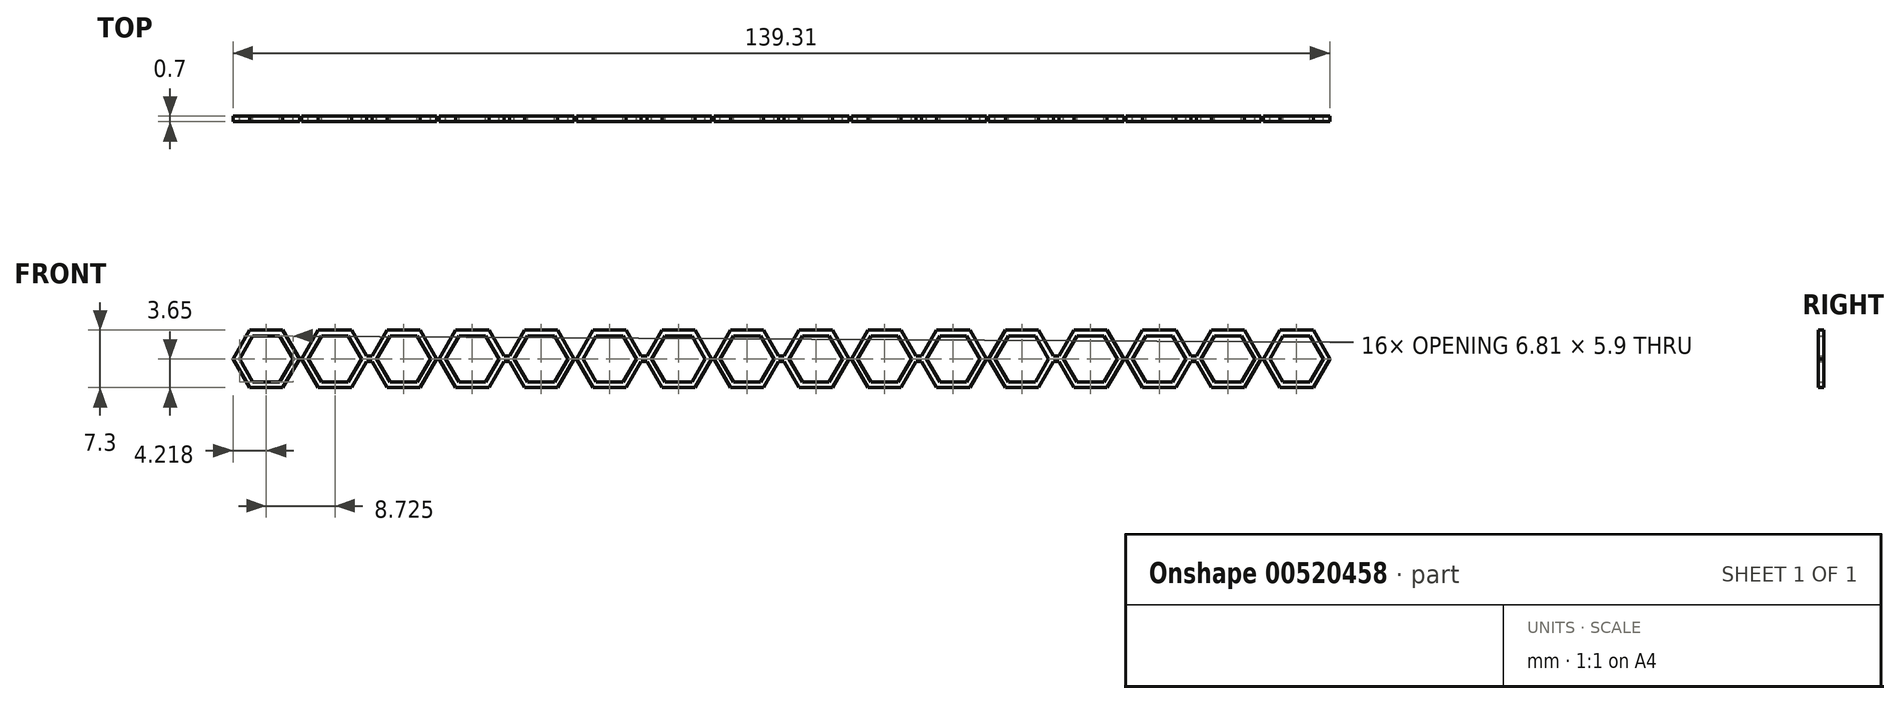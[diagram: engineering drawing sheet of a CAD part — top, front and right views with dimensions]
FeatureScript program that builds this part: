
annotation { "Feature Type Name" : "Feature", "Feature Type Description" : "" }
export const myFeature = defineFeature(function(context is Context, id is Id, definition is map)
    precondition{}
    {
        {
            var Q0;
            Q0=qCreatedBy(makeId("Front.planeOp"),FACE);
            var sketch = newSketch(context, id + "F0", { "sketchPlane" : qUnion([Q0])});
            skCircle(sketch, "E0.cCircle", {"center": v(0, 0) * mm, "radius": 2.95 * mm, "construction": true});
            skLineSegment(sketch, "E0.0", {"start": v(-1.7, 2.95) * mm, "end": v(1.7, 2.95) * mm});
            skLineSegment(sketch, "E0.1", {"start": v(1.7, 2.95) * mm, "end": v(3.4, 0) * mm});
            skLineSegment(sketch, "E0.2", {"start": v(3.4, 0) * mm, "end": v(1.7, -2.95) * mm});
            skLineSegment(sketch, "E0.3", {"start": v(1.7, -2.95) * mm, "end": v(-1.7, -2.95) * mm});
            skLineSegment(sketch, "E0.4", {"start": v(-1.7, -2.95) * mm, "end": v(-3.4, 0) * mm});
            skLineSegment(sketch, "E0.5", {"start": v(-3.4, 0) * mm, "end": v(-1.7, 2.95) * mm});
            skPoint(sketch, "E0.0.midPoint", {"position": v(0, 2.95) * mm});
            skCircle(sketch, "E1.cCircle", {"center": v(0, 0) * mm, "radius": 3.65 * mm, "construction": true});
            skLineSegment(sketch, "E1.0", {"start": v(-2.1, 3.65) * mm, "end": v(2.1, 3.65) * mm});
            skLineSegment(sketch, "E1.1", {"start": v(2.1, 3.65) * mm, "end": v(4.21, 0) * mm});
            skLineSegment(sketch, "E1.2", {"start": v(4.21, 0) * mm, "end": v(2.1, -3.65) * mm});
            skLineSegment(sketch, "E1.3", {"start": v(2.1, -3.65) * mm, "end": v(-2.1, -3.65) * mm});
            skLineSegment(sketch, "E1.4", {"start": v(-2.1, -3.65) * mm, "end": v(-4.21, 0) * mm});
            skLineSegment(sketch, "E1.5", {"start": v(-4.21, 0) * mm, "end": v(-2.1, 3.65) * mm});
            skPoint(sketch, "E1.0.midPoint", {"position": v(0, 3.65) * mm});
            skCircle(sketch, "E2.cCircle", {"center": v(8.73, 0) * mm, "radius": 2.95 * mm, "construction": true});
            skLineSegment(sketch, "E2.0", {"start": v(7.02, 2.95) * mm, "end": v(10.43, 2.95) * mm});
            skLineSegment(sketch, "E2.1", {"start": v(10.43, 2.95) * mm, "end": v(12.13, 0) * mm});
            skLineSegment(sketch, "E2.2", {"start": v(12.13, 0) * mm, "end": v(10.43, -2.95) * mm});
            skLineSegment(sketch, "E2.3", {"start": v(10.43, -2.95) * mm, "end": v(7.02, -2.95) * mm});
            skLineSegment(sketch, "E2.4", {"start": v(7.02, -2.95) * mm, "end": v(5.32, 0) * mm});
            skLineSegment(sketch, "E2.5", {"start": v(5.32, 0) * mm, "end": v(7.02, 2.95) * mm});
            skPoint(sketch, "E2.0.midPoint", {"position": v(8.73, 2.95) * mm});
            skCircle(sketch, "E3.cCircle", {"center": v(8.73, 0) * mm, "radius": 3.65 * mm, "construction": true});
            skLineSegment(sketch, "E3.0", {"start": v(6.62, 3.65) * mm, "end": v(10.83, 3.65) * mm});
            skLineSegment(sketch, "E3.1", {"start": v(10.83, 3.65) * mm, "end": v(12.94, 0) * mm});
            skLineSegment(sketch, "E3.2", {"start": v(12.94, 0) * mm, "end": v(10.83, -3.65) * mm});
            skLineSegment(sketch, "E3.3", {"start": v(10.83, -3.65) * mm, "end": v(6.62, -3.65) * mm});
            skLineSegment(sketch, "E3.4", {"start": v(6.62, -3.65) * mm, "end": v(4.51, 0) * mm});
            skLineSegment(sketch, "E3.5", {"start": v(4.51, 0) * mm, "end": v(6.62, 3.65) * mm});
            skPoint(sketch, "E3.0.midPoint", {"position": v(8.73, 3.65) * mm});
            skLineSegment(sketch, "E4", {"start": v(4.01, 0.35) * mm, "end": v(4.71, 0.35) * mm});
            skLineSegment(sketch, "E5", {"start": v(4.01, -0.35) * mm, "end": v(4.71, -0.35) * mm});
            skLineSegment(sketch, "E6", {"start": v(12.94, 0) * mm, "end": v(13.24, 0) * mm});
            skCircle(sketch, "E7.cCircle", {"center": v(17.45, 0) * mm, "radius": 2.95 * mm, "construction": true});
            skLineSegment(sketch, "E7.0", {"start": v(15.75, 2.95) * mm, "end": v(19.15, 2.95) * mm});
            skLineSegment(sketch, "E7.1", {"start": v(19.15, 2.95) * mm, "end": v(20.86, 0) * mm});
            skLineSegment(sketch, "E7.2", {"start": v(20.86, 0) * mm, "end": v(19.15, -2.95) * mm});
            skLineSegment(sketch, "E7.3", {"start": v(19.15, -2.95) * mm, "end": v(15.75, -2.95) * mm});
            skLineSegment(sketch, "E7.4", {"start": v(15.75, -2.95) * mm, "end": v(14.04, 0) * mm});
            skLineSegment(sketch, "E7.5", {"start": v(14.04, 0) * mm, "end": v(15.75, 2.95) * mm});
            skPoint(sketch, "E7.0.midPoint", {"position": v(17.45, 2.95) * mm});
            skCircle(sketch, "E8.cCircle", {"center": v(17.45, 0) * mm, "radius": 3.65 * mm, "construction": true});
            skLineSegment(sketch, "E8.0", {"start": v(15.34, 3.65) * mm, "end": v(19.56, 3.65) * mm});
            skLineSegment(sketch, "E8.1", {"start": v(19.56, 3.65) * mm, "end": v(21.67, 0) * mm});
            skLineSegment(sketch, "E8.2", {"start": v(21.67, 0) * mm, "end": v(19.56, -3.65) * mm});
            skLineSegment(sketch, "E8.3", {"start": v(19.56, -3.65) * mm, "end": v(15.34, -3.65) * mm});
            skLineSegment(sketch, "E8.4", {"start": v(15.34, -3.65) * mm, "end": v(13.24, 0) * mm});
            skLineSegment(sketch, "E8.5", {"start": v(13.24, 0) * mm, "end": v(15.34, 3.65) * mm});
            skPoint(sketch, "E8.0.midPoint", {"position": v(17.45, 3.65) * mm});
            skCircle(sketch, "E9.cCircle", {"center": v(26.18, 0) * mm, "radius": 2.95 * mm, "construction": true});
            skLineSegment(sketch, "E9.0", {"start": v(24.47, 2.95) * mm, "end": v(27.88, 2.95) * mm});
            skLineSegment(sketch, "E9.1", {"start": v(27.88, 2.95) * mm, "end": v(29.58, 0) * mm});
            skLineSegment(sketch, "E9.2", {"start": v(29.58, 0) * mm, "end": v(27.88, -2.95) * mm});
            skLineSegment(sketch, "E9.3", {"start": v(27.88, -2.95) * mm, "end": v(24.47, -2.95) * mm});
            skLineSegment(sketch, "E9.4", {"start": v(24.47, -2.95) * mm, "end": v(22.77, 0) * mm});
            skLineSegment(sketch, "E9.5", {"start": v(22.77, 0) * mm, "end": v(24.47, 2.95) * mm});
            skPoint(sketch, "E9.0.midPoint", {"position": v(26.18, 2.95) * mm});
            skCircle(sketch, "E10.cCircle", {"center": v(26.18, 0) * mm, "radius": 3.65 * mm, "construction": true});
            skLineSegment(sketch, "E10.0", {"start": v(24.07, 3.65) * mm, "end": v(28.28, 3.65) * mm});
            skLineSegment(sketch, "E10.1", {"start": v(28.28, 3.65) * mm, "end": v(30.4, 0) * mm});
            skLineSegment(sketch, "E10.2", {"start": v(30.4, 0) * mm, "end": v(28.28, -3.65) * mm});
            skLineSegment(sketch, "E10.3", {"start": v(28.28, -3.65) * mm, "end": v(24.07, -3.65) * mm});
            skLineSegment(sketch, "E10.4", {"start": v(24.07, -3.65) * mm, "end": v(21.96, 0) * mm});
            skLineSegment(sketch, "E10.5", {"start": v(21.96, 0) * mm, "end": v(24.07, 3.65) * mm});
            skPoint(sketch, "E10.0.midPoint", {"position": v(26.18, 3.65) * mm});
            skLineSegment(sketch, "E11", {"start": v(21.46, 0.35) * mm, "end": v(22.16, 0.35) * mm});
            skLineSegment(sketch, "E12", {"start": v(21.46, -0.35) * mm, "end": v(22.16, -0.35) * mm});
            skLineSegment(sketch, "E13", {"start": v(30.4, 0) * mm, "end": v(30.69, 0) * mm});
            skLineSegment(sketch, "E14", {"start": v(13.24, 0.35) * mm, "end": v(12.74, 0.35) * mm});
            skLineSegment(sketch, "E15", {"start": v(13.24, -0.35) * mm, "end": v(12.74, -0.35) * mm});
            skLineSegment(sketch, "E16", {"start": v(13.24, -0.35) * mm, "end": v(13.44, -0.35) * mm});
            skLineSegment(sketch, "E17", {"start": v(13.24, 0.35) * mm, "end": v(13.44, 0.35) * mm});
            skCircle(sketch, "E18.cCircle", {"center": v(34.9, 0) * mm, "radius": 2.95 * mm, "construction": true});
            skLineSegment(sketch, "E18.0", {"start": v(33.2, 2.95) * mm, "end": v(36.6, 2.95) * mm});
            skLineSegment(sketch, "E18.1", {"start": v(36.6, 2.95) * mm, "end": v(38.3, 0) * mm});
            skLineSegment(sketch, "E18.2", {"start": v(38.3, 0) * mm, "end": v(36.6, -2.95) * mm});
            skLineSegment(sketch, "E18.3", {"start": v(36.6, -2.95) * mm, "end": v(33.2, -2.95) * mm});
            skLineSegment(sketch, "E18.4", {"start": v(33.2, -2.95) * mm, "end": v(31.5, 0) * mm});
            skLineSegment(sketch, "E18.5", {"start": v(31.5, 0) * mm, "end": v(33.2, 2.95) * mm});
            skPoint(sketch, "E18.0.midPoint", {"position": v(34.9, 2.95) * mm});
            skCircle(sketch, "E19.cCircle", {"center": v(34.9, 0) * mm, "radius": 3.65 * mm, "construction": true});
            skLineSegment(sketch, "E19.0", {"start": v(32.8, 3.65) * mm, "end": v(37, 3.65) * mm});
            skLineSegment(sketch, "E19.1", {"start": v(37, 3.65) * mm, "end": v(39.12, 0) * mm});
            skLineSegment(sketch, "E19.2", {"start": v(39.12, 0) * mm, "end": v(37, -3.65) * mm});
            skLineSegment(sketch, "E19.3", {"start": v(37, -3.65) * mm, "end": v(32.8, -3.65) * mm});
            skLineSegment(sketch, "E19.4", {"start": v(32.8, -3.65) * mm, "end": v(30.69, 0) * mm});
            skLineSegment(sketch, "E19.5", {"start": v(30.69, 0) * mm, "end": v(32.8, 3.65) * mm});
            skPoint(sketch, "E19.0.midPoint", {"position": v(34.9, 3.65) * mm});
            skCircle(sketch, "E20.cCircle", {"center": v(43.63, 0) * mm, "radius": 2.95 * mm, "construction": true});
            skLineSegment(sketch, "E20.0", {"start": v(41.92, 2.95) * mm, "end": v(45.33, 2.95) * mm});
            skLineSegment(sketch, "E20.1", {"start": v(45.33, 2.95) * mm, "end": v(47.03, 0) * mm});
            skLineSegment(sketch, "E20.2", {"start": v(47.03, 0) * mm, "end": v(45.33, -2.95) * mm});
            skLineSegment(sketch, "E20.3", {"start": v(45.33, -2.95) * mm, "end": v(41.92, -2.95) * mm});
            skLineSegment(sketch, "E20.4", {"start": v(41.92, -2.95) * mm, "end": v(40.22, 0) * mm});
            skLineSegment(sketch, "E20.5", {"start": v(40.22, 0) * mm, "end": v(41.92, 2.95) * mm});
            skPoint(sketch, "E20.0.midPoint", {"position": v(43.63, 2.95) * mm});
            skCircle(sketch, "E21.cCircle", {"center": v(43.63, 0) * mm, "radius": 3.65 * mm, "construction": true});
            skLineSegment(sketch, "E21.0", {"start": v(41.52, 3.65) * mm, "end": v(45.73, 3.65) * mm});
            skLineSegment(sketch, "E21.1", {"start": v(45.73, 3.65) * mm, "end": v(47.84, 0) * mm});
            skLineSegment(sketch, "E21.2", {"start": v(47.84, 0) * mm, "end": v(45.73, -3.65) * mm});
            skLineSegment(sketch, "E21.3", {"start": v(45.73, -3.65) * mm, "end": v(41.52, -3.65) * mm});
            skLineSegment(sketch, "E21.4", {"start": v(41.52, -3.65) * mm, "end": v(39.41, 0) * mm});
            skLineSegment(sketch, "E21.5", {"start": v(39.41, 0) * mm, "end": v(41.52, 3.65) * mm});
            skPoint(sketch, "E21.0.midPoint", {"position": v(43.63, 3.65) * mm});
            skLineSegment(sketch, "E22", {"start": v(38.91, 0.35) * mm, "end": v(39.61, 0.35) * mm});
            skLineSegment(sketch, "E23", {"start": v(38.91, -0.35) * mm, "end": v(39.61, -0.35) * mm});
            skLineSegment(sketch, "E24", {"start": v(47.84, 0) * mm, "end": v(48.14, 0) * mm});
            skCircle(sketch, "E25.cCircle", {"center": v(52.35, 0) * mm, "radius": 2.95 * mm, "construction": true});
            skLineSegment(sketch, "E25.0", {"start": v(50.65, 2.95) * mm, "end": v(54.06, 2.95) * mm});
            skLineSegment(sketch, "E25.1", {"start": v(54.06, 2.95) * mm, "end": v(55.76, 0) * mm});
            skLineSegment(sketch, "E25.2", {"start": v(55.76, 0) * mm, "end": v(54.06, -2.95) * mm});
            skLineSegment(sketch, "E25.3", {"start": v(54.06, -2.95) * mm, "end": v(50.65, -2.95) * mm});
            skLineSegment(sketch, "E25.4", {"start": v(50.65, -2.95) * mm, "end": v(48.95, 0) * mm});
            skLineSegment(sketch, "E25.5", {"start": v(48.95, 0) * mm, "end": v(50.65, 2.95) * mm});
            skPoint(sketch, "E25.0.midPoint", {"position": v(52.35, 2.95) * mm});
            skCircle(sketch, "E26.cCircle", {"center": v(52.35, 0) * mm, "radius": 3.65 * mm, "construction": true});
            skLineSegment(sketch, "E26.0", {"start": v(50.24, 3.65) * mm, "end": v(54.46, 3.65) * mm});
            skLineSegment(sketch, "E26.1", {"start": v(54.46, 3.65) * mm, "end": v(56.57, 0) * mm});
            skLineSegment(sketch, "E26.2", {"start": v(56.57, 0) * mm, "end": v(54.46, -3.65) * mm});
            skLineSegment(sketch, "E26.3", {"start": v(54.46, -3.65) * mm, "end": v(50.24, -3.65) * mm});
            skLineSegment(sketch, "E26.4", {"start": v(50.24, -3.65) * mm, "end": v(48.14, 0) * mm});
            skLineSegment(sketch, "E26.5", {"start": v(48.14, 0) * mm, "end": v(50.24, 3.65) * mm});
            skPoint(sketch, "E26.0.midPoint", {"position": v(52.35, 3.65) * mm});
            skCircle(sketch, "E27.cCircle", {"center": v(61.08, 0) * mm, "radius": 2.95 * mm, "construction": true});
            skLineSegment(sketch, "E27.0", {"start": v(59.37, 2.95) * mm, "end": v(62.78, 2.95) * mm});
            skLineSegment(sketch, "E27.1", {"start": v(62.78, 2.95) * mm, "end": v(64.48, 0) * mm});
            skLineSegment(sketch, "E27.2", {"start": v(64.48, 0) * mm, "end": v(62.78, -2.95) * mm});
            skLineSegment(sketch, "E27.3", {"start": v(62.78, -2.95) * mm, "end": v(59.37, -2.95) * mm});
            skLineSegment(sketch, "E27.4", {"start": v(59.37, -2.95) * mm, "end": v(57.67, 0) * mm});
            skLineSegment(sketch, "E27.5", {"start": v(57.67, 0) * mm, "end": v(59.37, 2.95) * mm});
            skPoint(sketch, "E27.0.midPoint", {"position": v(61.08, 2.95) * mm});
            skCircle(sketch, "E28.cCircle", {"center": v(61.08, 0) * mm, "radius": 3.65 * mm, "construction": true});
            skLineSegment(sketch, "E28.0", {"start": v(58.97, 3.65) * mm, "end": v(63.18, 3.65) * mm});
            skLineSegment(sketch, "E28.1", {"start": v(63.18, 3.65) * mm, "end": v(65.3, 0) * mm});
            skLineSegment(sketch, "E28.2", {"start": v(65.3, 0) * mm, "end": v(63.18, -3.65) * mm});
            skLineSegment(sketch, "E28.3", {"start": v(63.18, -3.65) * mm, "end": v(58.97, -3.65) * mm});
            skLineSegment(sketch, "E28.4", {"start": v(58.97, -3.65) * mm, "end": v(56.86, 0) * mm});
            skLineSegment(sketch, "E28.5", {"start": v(56.86, 0) * mm, "end": v(58.97, 3.65) * mm});
            skPoint(sketch, "E28.0.midPoint", {"position": v(61.08, 3.65) * mm});
            skLineSegment(sketch, "E29", {"start": v(56.36, 0.35) * mm, "end": v(57.06, 0.35) * mm});
            skLineSegment(sketch, "E30", {"start": v(56.36, -0.35) * mm, "end": v(57.06, -0.35) * mm});
            skLineSegment(sketch, "E31", {"start": v(65.3, 0) * mm, "end": v(65.59, 0) * mm});
            skLineSegment(sketch, "E32", {"start": v(65.59, 0) * mm, "end": v(65.59, 0.35) * mm});
            skLineSegment(sketch, "E33", {"start": v(65.59, 0) * mm, "end": v(65.59, -0.35) * mm});
            skLineSegment(sketch, "E34", {"start": v(48.14, 0.35) * mm, "end": v(47.64, 0.35) * mm});
            skLineSegment(sketch, "E35", {"start": v(48.14, -0.35) * mm, "end": v(47.64, -0.35) * mm});
            skLineSegment(sketch, "E36", {"start": v(48.14, -0.35) * mm, "end": v(48.34, -0.35) * mm});
            skLineSegment(sketch, "E37", {"start": v(48.14, 0.35) * mm, "end": v(48.34, 0.35) * mm});
            skLineSegment(sketch, "E38", {"start": v(30.69, 0.35) * mm, "end": v(30.19, 0.35) * mm});
            skLineSegment(sketch, "E39", {"start": v(30.69, -0.35) * mm, "end": v(30.19, -0.35) * mm});
            skLineSegment(sketch, "E40", {"start": v(30.69, -0.35) * mm, "end": v(30.89, -0.35) * mm});
            skLineSegment(sketch, "E41", {"start": v(30.69, 0.35) * mm, "end": v(30.89, 0.35) * mm});
            skCircle(sketch, "E42.cCircle", {"center": v(-69.8, 0) * mm, "radius": 2.95 * mm, "construction": true});
            skLineSegment(sketch, "E42.0", {"start": v(-71.5, 2.95) * mm, "end": v(-68.1, 2.95) * mm});
            skLineSegment(sketch, "E42.1", {"start": v(-68.1, 2.95) * mm, "end": v(-66.4, 0) * mm});
            skLineSegment(sketch, "E42.2", {"start": v(-66.4, 0) * mm, "end": v(-68.1, -2.95) * mm});
            skLineSegment(sketch, "E42.3", {"start": v(-68.1, -2.95) * mm, "end": v(-71.5, -2.95) * mm});
            skLineSegment(sketch, "E42.4", {"start": v(-71.5, -2.95) * mm, "end": v(-73.2, 0) * mm});
            skLineSegment(sketch, "E42.5", {"start": v(-73.2, 0) * mm, "end": v(-71.5, 2.95) * mm});
            skPoint(sketch, "E42.0.midPoint", {"position": v(-69.8, 2.95) * mm});
            skCircle(sketch, "E43.cCircle", {"center": v(-69.8, 0) * mm, "radius": 3.65 * mm, "construction": true});
            skLineSegment(sketch, "E43.0", {"start": v(-71.9, 3.65) * mm, "end": v(-67.7, 3.65) * mm});
            skLineSegment(sketch, "E43.1", {"start": v(-67.7, 3.65) * mm, "end": v(-65.59, 0) * mm});
            skLineSegment(sketch, "E43.2", {"start": v(-65.59, 0) * mm, "end": v(-67.7, -3.65) * mm});
            skLineSegment(sketch, "E43.3", {"start": v(-67.7, -3.65) * mm, "end": v(-71.9, -3.65) * mm});
            skLineSegment(sketch, "E43.4", {"start": v(-71.9, -3.65) * mm, "end": v(-74.02, 0) * mm});
            skLineSegment(sketch, "E43.5", {"start": v(-74.02, 0) * mm, "end": v(-71.9, 3.65) * mm});
            skPoint(sketch, "E43.0.midPoint", {"position": v(-69.8, 3.65) * mm});
            skCircle(sketch, "E44.cCircle", {"center": v(-61.08, 0) * mm, "radius": 2.95 * mm, "construction": true});
            skLineSegment(sketch, "E44.0", {"start": v(-62.78, 2.95) * mm, "end": v(-59.37, 2.95) * mm});
            skLineSegment(sketch, "E44.1", {"start": v(-59.37, 2.95) * mm, "end": v(-57.67, 0) * mm});
            skLineSegment(sketch, "E44.2", {"start": v(-57.67, 0) * mm, "end": v(-59.37, -2.95) * mm});
            skLineSegment(sketch, "E44.3", {"start": v(-59.37, -2.95) * mm, "end": v(-62.78, -2.95) * mm});
            skLineSegment(sketch, "E44.4", {"start": v(-62.78, -2.95) * mm, "end": v(-64.48, 0) * mm});
            skLineSegment(sketch, "E44.5", {"start": v(-64.48, 0) * mm, "end": v(-62.78, 2.95) * mm});
            skPoint(sketch, "E44.0.midPoint", {"position": v(-61.08, 2.95) * mm});
            skCircle(sketch, "E45.cCircle", {"center": v(-61.08, 0) * mm, "radius": 3.65 * mm, "construction": true});
            skLineSegment(sketch, "E45.0", {"start": v(-63.18, 3.65) * mm, "end": v(-58.97, 3.65) * mm});
            skLineSegment(sketch, "E45.1", {"start": v(-58.97, 3.65) * mm, "end": v(-56.86, 0) * mm});
            skLineSegment(sketch, "E45.2", {"start": v(-56.86, 0) * mm, "end": v(-58.97, -3.65) * mm});
            skLineSegment(sketch, "E45.3", {"start": v(-58.97, -3.65) * mm, "end": v(-63.18, -3.65) * mm});
            skLineSegment(sketch, "E45.4", {"start": v(-63.18, -3.65) * mm, "end": v(-65.3, 0) * mm});
            skLineSegment(sketch, "E45.5", {"start": v(-65.3, 0) * mm, "end": v(-63.18, 3.65) * mm});
            skPoint(sketch, "E45.0.midPoint", {"position": v(-61.08, 3.65) * mm});
            skLineSegment(sketch, "E46", {"start": v(-65.79, 0.35) * mm, "end": v(-65.09, 0.35) * mm});
            skLineSegment(sketch, "E47", {"start": v(-65.79, -0.35) * mm, "end": v(-65.09, -0.35) * mm});
            skLineSegment(sketch, "E48", {"start": v(-56.86, 0) * mm, "end": v(-56.57, 0) * mm});
            skCircle(sketch, "E49.cCircle", {"center": v(-52.35, 0) * mm, "radius": 2.95 * mm, "construction": true});
            skLineSegment(sketch, "E49.0", {"start": v(-54.05, 2.95) * mm, "end": v(-50.65, 2.95) * mm});
            skLineSegment(sketch, "E49.1", {"start": v(-50.65, 2.95) * mm, "end": v(-48.95, 0) * mm});
            skLineSegment(sketch, "E49.2", {"start": v(-48.95, 0) * mm, "end": v(-50.65, -2.95) * mm});
            skLineSegment(sketch, "E49.3", {"start": v(-50.65, -2.95) * mm, "end": v(-54.05, -2.95) * mm});
            skLineSegment(sketch, "E49.4", {"start": v(-54.05, -2.95) * mm, "end": v(-55.76, 0) * mm});
            skLineSegment(sketch, "E49.5", {"start": v(-55.76, 0) * mm, "end": v(-54.05, 2.95) * mm});
            skPoint(sketch, "E49.0.midPoint", {"position": v(-52.35, 2.95) * mm});
            skCircle(sketch, "E50.cCircle", {"center": v(-52.35, 0) * mm, "radius": 3.65 * mm, "construction": true});
            skLineSegment(sketch, "E50.0", {"start": v(-54.46, 3.65) * mm, "end": v(-50.24, 3.65) * mm});
            skLineSegment(sketch, "E50.1", {"start": v(-50.24, 3.65) * mm, "end": v(-48.14, 0) * mm});
            skLineSegment(sketch, "E50.2", {"start": v(-48.14, 0) * mm, "end": v(-50.24, -3.65) * mm});
            skLineSegment(sketch, "E50.3", {"start": v(-50.24, -3.65) * mm, "end": v(-54.46, -3.65) * mm});
            skLineSegment(sketch, "E50.4", {"start": v(-54.46, -3.65) * mm, "end": v(-56.57, 0) * mm});
            skLineSegment(sketch, "E50.5", {"start": v(-56.57, 0) * mm, "end": v(-54.46, 3.65) * mm});
            skPoint(sketch, "E50.0.midPoint", {"position": v(-52.35, 3.65) * mm});
            skCircle(sketch, "E51.cCircle", {"center": v(-43.63, 0) * mm, "radius": 2.95 * mm, "construction": true});
            skLineSegment(sketch, "E51.0", {"start": v(-45.33, 2.95) * mm, "end": v(-41.92, 2.95) * mm});
            skLineSegment(sketch, "E51.1", {"start": v(-41.92, 2.95) * mm, "end": v(-40.22, 0) * mm});
            skLineSegment(sketch, "E51.2", {"start": v(-40.22, 0) * mm, "end": v(-41.92, -2.95) * mm});
            skLineSegment(sketch, "E51.3", {"start": v(-41.92, -2.95) * mm, "end": v(-45.33, -2.95) * mm});
            skLineSegment(sketch, "E51.4", {"start": v(-45.33, -2.95) * mm, "end": v(-47.03, 0) * mm});
            skLineSegment(sketch, "E51.5", {"start": v(-47.03, 0) * mm, "end": v(-45.33, 2.95) * mm});
            skPoint(sketch, "E51.0.midPoint", {"position": v(-43.63, 2.95) * mm});
            skCircle(sketch, "E52.cCircle", {"center": v(-43.63, 0) * mm, "radius": 3.65 * mm, "construction": true});
            skLineSegment(sketch, "E52.0", {"start": v(-45.73, 3.65) * mm, "end": v(-41.52, 3.65) * mm});
            skLineSegment(sketch, "E52.1", {"start": v(-41.52, 3.65) * mm, "end": v(-39.41, 0) * mm});
            skLineSegment(sketch, "E52.2", {"start": v(-39.41, 0) * mm, "end": v(-41.52, -3.65) * mm});
            skLineSegment(sketch, "E52.3", {"start": v(-41.52, -3.65) * mm, "end": v(-45.73, -3.65) * mm});
            skLineSegment(sketch, "E52.4", {"start": v(-45.73, -3.65) * mm, "end": v(-47.84, 0) * mm});
            skLineSegment(sketch, "E52.5", {"start": v(-47.84, 0) * mm, "end": v(-45.73, 3.65) * mm});
            skPoint(sketch, "E52.0.midPoint", {"position": v(-43.63, 3.65) * mm});
            skLineSegment(sketch, "E53", {"start": v(-48.34, 0.35) * mm, "end": v(-47.64, 0.35) * mm});
            skLineSegment(sketch, "E54", {"start": v(-48.34, -0.35) * mm, "end": v(-47.64, -0.35) * mm});
            skLineSegment(sketch, "E55", {"start": v(-39.41, 0) * mm, "end": v(-39.12, 0) * mm});
            skLineSegment(sketch, "E56", {"start": v(-56.57, 0.35) * mm, "end": v(-57.06, 0.35) * mm});
            skLineSegment(sketch, "E57", {"start": v(-56.57, -0.35) * mm, "end": v(-57.06, -0.35) * mm});
            skLineSegment(sketch, "E58", {"start": v(-56.57, -0.35) * mm, "end": v(-56.36, -0.35) * mm});
            skLineSegment(sketch, "E59", {"start": v(-56.57, 0.35) * mm, "end": v(-56.36, 0.35) * mm});
            skCircle(sketch, "E60.cCircle", {"center": v(-34.9, 0) * mm, "radius": 2.95 * mm, "construction": true});
            skLineSegment(sketch, "E60.0", {"start": v(-36.6, 2.95) * mm, "end": v(-33.2, 2.95) * mm});
            skLineSegment(sketch, "E60.1", {"start": v(-33.2, 2.95) * mm, "end": v(-31.5, 0) * mm});
            skLineSegment(sketch, "E60.2", {"start": v(-31.5, 0) * mm, "end": v(-33.2, -2.95) * mm});
            skLineSegment(sketch, "E60.3", {"start": v(-33.2, -2.95) * mm, "end": v(-36.6, -2.95) * mm});
            skLineSegment(sketch, "E60.4", {"start": v(-36.6, -2.95) * mm, "end": v(-38.3, 0) * mm});
            skLineSegment(sketch, "E60.5", {"start": v(-38.3, 0) * mm, "end": v(-36.6, 2.95) * mm});
            skPoint(sketch, "E60.0.midPoint", {"position": v(-34.9, 2.95) * mm});
            skCircle(sketch, "E61.cCircle", {"center": v(-34.9, 0) * mm, "radius": 3.65 * mm, "construction": true});
            skLineSegment(sketch, "E61.0", {"start": v(-37, 3.65) * mm, "end": v(-32.8, 3.65) * mm});
            skLineSegment(sketch, "E61.1", {"start": v(-32.8, 3.65) * mm, "end": v(-30.69, 0) * mm});
            skLineSegment(sketch, "E61.2", {"start": v(-30.69, 0) * mm, "end": v(-32.8, -3.65) * mm});
            skLineSegment(sketch, "E61.3", {"start": v(-32.8, -3.65) * mm, "end": v(-37, -3.65) * mm});
            skLineSegment(sketch, "E61.4", {"start": v(-37, -3.65) * mm, "end": v(-39.12, 0) * mm});
            skLineSegment(sketch, "E61.5", {"start": v(-39.12, 0) * mm, "end": v(-37, 3.65) * mm});
            skPoint(sketch, "E61.0.midPoint", {"position": v(-34.9, 3.65) * mm});
            skCircle(sketch, "E62.cCircle", {"center": v(-26.18, 0) * mm, "radius": 2.95 * mm, "construction": true});
            skLineSegment(sketch, "E62.0", {"start": v(-27.88, 2.95) * mm, "end": v(-24.47, 2.95) * mm});
            skLineSegment(sketch, "E62.1", {"start": v(-24.47, 2.95) * mm, "end": v(-22.77, 0) * mm});
            skLineSegment(sketch, "E62.2", {"start": v(-22.77, 0) * mm, "end": v(-24.47, -2.95) * mm});
            skLineSegment(sketch, "E62.3", {"start": v(-24.47, -2.95) * mm, "end": v(-27.88, -2.95) * mm});
            skLineSegment(sketch, "E62.4", {"start": v(-27.88, -2.95) * mm, "end": v(-29.58, 0) * mm});
            skLineSegment(sketch, "E62.5", {"start": v(-29.58, 0) * mm, "end": v(-27.88, 2.95) * mm});
            skPoint(sketch, "E62.0.midPoint", {"position": v(-26.18, 2.95) * mm});
            skCircle(sketch, "E63.cCircle", {"center": v(-26.18, 0) * mm, "radius": 3.65 * mm, "construction": true});
            skLineSegment(sketch, "E63.0", {"start": v(-28.28, 3.65) * mm, "end": v(-24.07, 3.65) * mm});
            skLineSegment(sketch, "E63.1", {"start": v(-24.07, 3.65) * mm, "end": v(-21.96, 0) * mm});
            skLineSegment(sketch, "E63.2", {"start": v(-21.96, 0) * mm, "end": v(-24.07, -3.65) * mm});
            skLineSegment(sketch, "E63.3", {"start": v(-24.07, -3.65) * mm, "end": v(-28.28, -3.65) * mm});
            skLineSegment(sketch, "E63.4", {"start": v(-28.28, -3.65) * mm, "end": v(-30.4, 0) * mm});
            skLineSegment(sketch, "E63.5", {"start": v(-30.4, 0) * mm, "end": v(-28.28, 3.65) * mm});
            skPoint(sketch, "E63.0.midPoint", {"position": v(-26.18, 3.65) * mm});
            skLineSegment(sketch, "E64", {"start": v(-30.89, 0.35) * mm, "end": v(-30.19, 0.35) * mm});
            skLineSegment(sketch, "E65", {"start": v(-30.89, -0.35) * mm, "end": v(-30.19, -0.35) * mm});
            skLineSegment(sketch, "E66", {"start": v(-21.96, 0) * mm, "end": v(-21.66, 0) * mm});
            skCircle(sketch, "E67.cCircle", {"center": v(-17.45, 0) * mm, "radius": 2.95 * mm, "construction": true});
            skLineSegment(sketch, "E67.0", {"start": v(-19.15, 2.95) * mm, "end": v(-15.75, 2.95) * mm});
            skLineSegment(sketch, "E67.1", {"start": v(-15.75, 2.95) * mm, "end": v(-14.04, 0) * mm});
            skLineSegment(sketch, "E67.2", {"start": v(-14.04, 0) * mm, "end": v(-15.75, -2.95) * mm});
            skLineSegment(sketch, "E67.3", {"start": v(-15.75, -2.95) * mm, "end": v(-19.15, -2.95) * mm});
            skLineSegment(sketch, "E67.4", {"start": v(-19.15, -2.95) * mm, "end": v(-20.86, 0) * mm});
            skLineSegment(sketch, "E67.5", {"start": v(-20.86, 0) * mm, "end": v(-19.15, 2.95) * mm});
            skPoint(sketch, "E67.0.midPoint", {"position": v(-17.45, 2.95) * mm});
            skCircle(sketch, "E68.cCircle", {"center": v(-17.45, 0) * mm, "radius": 3.65 * mm, "construction": true});
            skLineSegment(sketch, "E68.0", {"start": v(-19.56, 3.65) * mm, "end": v(-15.34, 3.65) * mm});
            skLineSegment(sketch, "E68.1", {"start": v(-15.34, 3.65) * mm, "end": v(-13.24, 0) * mm});
            skLineSegment(sketch, "E68.2", {"start": v(-13.24, 0) * mm, "end": v(-15.34, -3.65) * mm});
            skLineSegment(sketch, "E68.3", {"start": v(-15.34, -3.65) * mm, "end": v(-19.56, -3.65) * mm});
            skLineSegment(sketch, "E68.4", {"start": v(-19.56, -3.65) * mm, "end": v(-21.66, 0) * mm});
            skLineSegment(sketch, "E68.5", {"start": v(-21.66, 0) * mm, "end": v(-19.56, 3.65) * mm});
            skPoint(sketch, "E68.0.midPoint", {"position": v(-17.45, 3.65) * mm});
            skCircle(sketch, "E69.cCircle", {"center": v(-8.72, 0) * mm, "radius": 2.95 * mm, "construction": true});
            skLineSegment(sketch, "E69.0", {"start": v(-10.43, 2.95) * mm, "end": v(-7.02, 2.95) * mm});
            skLineSegment(sketch, "E69.1", {"start": v(-7.02, 2.95) * mm, "end": v(-5.32, 0) * mm});
            skLineSegment(sketch, "E69.2", {"start": v(-5.32, 0) * mm, "end": v(-7.02, -2.95) * mm});
            skLineSegment(sketch, "E69.3", {"start": v(-7.02, -2.95) * mm, "end": v(-10.43, -2.95) * mm});
            skLineSegment(sketch, "E69.4", {"start": v(-10.43, -2.95) * mm, "end": v(-12.13, 0) * mm});
            skLineSegment(sketch, "E69.5", {"start": v(-12.13, 0) * mm, "end": v(-10.43, 2.95) * mm});
            skPoint(sketch, "E69.0.midPoint", {"position": v(-8.72, 2.95) * mm});
            skCircle(sketch, "E70.cCircle", {"center": v(-8.72, 0) * mm, "radius": 3.65 * mm, "construction": true});
            skLineSegment(sketch, "E70.0", {"start": v(-10.83, 3.65) * mm, "end": v(-6.62, 3.65) * mm});
            skLineSegment(sketch, "E70.1", {"start": v(-6.62, 3.65) * mm, "end": v(-4.51, 0) * mm});
            skLineSegment(sketch, "E70.2", {"start": v(-4.51, 0) * mm, "end": v(-6.62, -3.65) * mm});
            skLineSegment(sketch, "E70.3", {"start": v(-6.62, -3.65) * mm, "end": v(-10.83, -3.65) * mm});
            skLineSegment(sketch, "E70.4", {"start": v(-10.83, -3.65) * mm, "end": v(-12.94, 0) * mm});
            skLineSegment(sketch, "E70.5", {"start": v(-12.94, 0) * mm, "end": v(-10.83, 3.65) * mm});
            skPoint(sketch, "E70.0.midPoint", {"position": v(-8.72, 3.65) * mm});
            skLineSegment(sketch, "E71", {"start": v(-13.44, 0.35) * mm, "end": v(-12.74, 0.35) * mm});
            skLineSegment(sketch, "E72", {"start": v(-13.44, -0.35) * mm, "end": v(-12.74, -0.35) * mm});
            skLineSegment(sketch, "E73", {"start": v(-4.51, 0) * mm, "end": v(-4.21, 0) * mm});
            skLineSegment(sketch, "E74", {"start": v(-21.66, 0.35) * mm, "end": v(-22.16, 0.35) * mm});
            skLineSegment(sketch, "E75", {"start": v(-21.66, -0.35) * mm, "end": v(-22.16, -0.35) * mm});
            skLineSegment(sketch, "E76", {"start": v(-21.66, -0.35) * mm, "end": v(-21.46, -0.35) * mm});
            skLineSegment(sketch, "E77", {"start": v(-21.66, 0.35) * mm, "end": v(-21.46, 0.35) * mm});
            skLineSegment(sketch, "E78", {"start": v(-39.12, 0.35) * mm, "end": v(-39.61, 0.35) * mm});
            skLineSegment(sketch, "E79", {"start": v(-39.12, -0.35) * mm, "end": v(-39.61, -0.35) * mm});
            skLineSegment(sketch, "E80", {"start": v(-39.12, -0.35) * mm, "end": v(-38.91, -0.35) * mm});
            skLineSegment(sketch, "E81", {"start": v(-39.12, 0.35) * mm, "end": v(-38.91, 0.35) * mm});
            skLineSegment(sketch, "E82", {"start": v(-4.21, 0.35) * mm, "end": v(-4.71, 0.35) * mm});
            skLineSegment(sketch, "E83", {"start": v(-4.21, 0.35) * mm, "end": v(-4.01, 0.35) * mm});
            skLineSegment(sketch, "E84", {"start": v(-4.21, -0.35) * mm, "end": v(-4.01, -0.35) * mm});
            skLineSegment(sketch, "E85", {"start": v(-4.21, -0.35) * mm, "end": v(-4.71, -0.35) * mm});
            skSolve(sketch);
        }
        {
            var Q0;
            Q0=makeQuery(id+"F0.imprint","IMPRINT",FACE,{"disambiguationData":[TD([[makeQuery(id+"F0.imprint","IMPRINT",EDGE,{"derivedFrom":sQuery(id+"F0.wireOp",EDGE,"E42.0")}),1.0]])]});
            var Q1;
            Q1=makeQuery(id+"F0.imprint","IMPRINT",FACE,{"disambiguationData":[TD([[makeQuery(id+"F0.imprint","IMPRINT",EDGE,{"derivedFrom":sQuery(id+"F0.wireOp",EDGE,"E44.0")}),1.0]])]});
            var Q2;
            {var subQ7=sQuery(id+"F0.wireOp",EDGE,"E46");Q2=makeQuery(id+"F0.imprint","IMPRINT",FACE,{"disambiguationData":[TD([[makeQuery(id+"F0.imprint","IMPRINT",EDGE,{"derivedFrom":subQ7}),-1.0]])]});}
            var Q3;
            {var subQ2=sQuery(id+"F0.wireOp",EDGE,"E48");Q3=makeQuery(id+"F0.imprint","IMPRINT",FACE,{"disambiguationData":[TD([[makeQuery(id+"F0.imprint","IMPRINT",EDGE,{"derivedFrom":subQ2}),-1.0]])]});}
            var Q4;
            {var subQ2=sQuery(id+"F0.wireOp",EDGE,"E48");Q4=makeQuery(id+"F0.imprint","IMPRINT",FACE,{"disambiguationData":[TD([[makeQuery(id+"F0.imprint","IMPRINT",EDGE,{"derivedFrom":subQ2}),1.0]])]});}
            var Q5;
            Q5=makeQuery(id+"F0.imprint","IMPRINT",FACE,{"disambiguationData":[TD([[makeQuery(id+"F0.imprint","IMPRINT",EDGE,{"derivedFrom":sQuery(id+"F0.wireOp",EDGE,"E49.0")}),1.0]])]});
            var Q6;
            {var subQ3=sQuery(id+"F0.wireOp",EDGE,"E53");Q6=makeQuery(id+"F0.imprint","IMPRINT",FACE,{"disambiguationData":[TD([[makeQuery(id+"F0.imprint","IMPRINT",EDGE,{"derivedFrom":subQ3}),-1.0]])]});}
            var Q7;
            Q7=makeQuery(id+"F0.imprint","IMPRINT",FACE,{"disambiguationData":[TD([[makeQuery(id+"F0.imprint","IMPRINT",EDGE,{"derivedFrom":sQuery(id+"F0.wireOp",EDGE,"E51.0")}),1.0]])]});
            var Q8;
            {var subQ1=sQuery(id+"F0.wireOp",EDGE,"E55");Q8=makeQuery(id+"F0.imprint","IMPRINT",FACE,{"disambiguationData":[TD([[makeQuery(id+"F0.imprint","IMPRINT",EDGE,{"derivedFrom":subQ1}),-1.0]])]});}
            var Q9;
            {var subQ2=sQuery(id+"F0.wireOp",EDGE,"E55");Q9=makeQuery(id+"F0.imprint","IMPRINT",FACE,{"disambiguationData":[TD([[makeQuery(id+"F0.imprint","IMPRINT",EDGE,{"derivedFrom":subQ2}),1.0]])]});}
            var Q10;
            Q10=makeQuery(id+"F0.imprint","IMPRINT",FACE,{"disambiguationData":[TD([[makeQuery(id+"F0.imprint","IMPRINT",EDGE,{"derivedFrom":sQuery(id+"F0.wireOp",EDGE,"E60.0")}),1.0]])]});
            var Q11;
            {var subQ3=sQuery(id+"F0.wireOp",EDGE,"E64");Q11=makeQuery(id+"F0.imprint","IMPRINT",FACE,{"disambiguationData":[TD([[makeQuery(id+"F0.imprint","IMPRINT",EDGE,{"derivedFrom":subQ3}),-1.0]])]});}
            var Q12;
            Q12=makeQuery(id+"F0.imprint","IMPRINT",FACE,{"disambiguationData":[TD([[makeQuery(id+"F0.imprint","IMPRINT",EDGE,{"derivedFrom":sQuery(id+"F0.wireOp",EDGE,"E62.0")}),1.0]])]});
            var Q13;
            {var subQ2=sQuery(id+"F0.wireOp",EDGE,"E66");Q13=makeQuery(id+"F0.imprint","IMPRINT",FACE,{"disambiguationData":[TD([[makeQuery(id+"F0.imprint","IMPRINT",EDGE,{"derivedFrom":subQ2}),1.0]])]});}
            var Q14;
            {var subQ2=sQuery(id+"F0.wireOp",EDGE,"E66");Q14=makeQuery(id+"F0.imprint","IMPRINT",FACE,{"disambiguationData":[TD([[makeQuery(id+"F0.imprint","IMPRINT",EDGE,{"derivedFrom":subQ2}),-1.0]])]});}
            var Q15;
            Q15=makeQuery(id+"F0.imprint","IMPRINT",FACE,{"disambiguationData":[TD([[makeQuery(id+"F0.imprint","IMPRINT",EDGE,{"derivedFrom":sQuery(id+"F0.wireOp",EDGE,"E67.0")}),1.0]])]});
            var Q16;
            Q16=makeQuery(id+"F0.imprint","IMPRINT",FACE,{"disambiguationData":[TD([[makeQuery(id+"F0.imprint","IMPRINT",EDGE,{"derivedFrom":sQuery(id+"F0.wireOp",EDGE,"E69.0")}),1.0]])]});
            var Q17;
            {var subQ3=sQuery(id+"F0.wireOp",EDGE,"E71");Q17=makeQuery(id+"F0.imprint","IMPRINT",FACE,{"disambiguationData":[TD([[makeQuery(id+"F0.imprint","IMPRINT",EDGE,{"derivedFrom":subQ3}),-1.0]])]});}
            var Q18;
            {var subQ5=sQuery(id+"F0.wireOp",EDGE,"E82");Q18=makeQuery(id+"F0.imprint","IMPRINT",FACE,{"disambiguationData":[TD([[makeQuery(id+"F0.imprint","IMPRINT",EDGE,{"derivedFrom":subQ5}),1.0]])]});}
            var Q19;
            {var subQ5=sQuery(id+"F0.wireOp",EDGE,"E84");Q19=makeQuery(id+"F0.imprint","IMPRINT",FACE,{"disambiguationData":[TD([[makeQuery(id+"F0.imprint","IMPRINT",EDGE,{"derivedFrom":subQ5}),1.0]])]});}
            var Q20;
            Q20=makeQuery(id+"F0.imprint","IMPRINT",FACE,{"disambiguationData":[TD([[makeQuery(id+"F0.imprint","IMPRINT",EDGE,{"derivedFrom":sQuery(id+"F0.wireOp",EDGE,"E0.0")}),1.0]])]});
            var Q21;
            {var subQ3=sQuery(id+"F0.wireOp",EDGE,"E4");Q21=makeQuery(id+"F0.imprint","IMPRINT",FACE,{"disambiguationData":[TD([[makeQuery(id+"F0.imprint","IMPRINT",EDGE,{"derivedFrom":subQ3}),-1.0]])]});}
            var Q22;
            Q22=makeQuery(id+"F0.imprint","IMPRINT",FACE,{"disambiguationData":[TD([[makeQuery(id+"F0.imprint","IMPRINT",EDGE,{"derivedFrom":sQuery(id+"F0.wireOp",EDGE,"E2.0")}),1.0]])]});
            var Q23;
            {var subQ2=sQuery(id+"F0.wireOp",EDGE,"E6");Q23=makeQuery(id+"F0.imprint","IMPRINT",FACE,{"disambiguationData":[TD([[makeQuery(id+"F0.imprint","IMPRINT",EDGE,{"derivedFrom":subQ2}),1.0]])]});}
            var Q24;
            {var subQ2=sQuery(id+"F0.wireOp",EDGE,"E6");Q24=makeQuery(id+"F0.imprint","IMPRINT",FACE,{"disambiguationData":[TD([[makeQuery(id+"F0.imprint","IMPRINT",EDGE,{"derivedFrom":subQ2}),-1.0]])]});}
            var Q25;
            Q25=makeQuery(id+"F0.imprint","IMPRINT",FACE,{"disambiguationData":[TD([[makeQuery(id+"F0.imprint","IMPRINT",EDGE,{"derivedFrom":sQuery(id+"F0.wireOp",EDGE,"E7.0")}),1.0]])]});
            var Q26;
            {var subQ3=sQuery(id+"F0.wireOp",EDGE,"E11");Q26=makeQuery(id+"F0.imprint","IMPRINT",FACE,{"disambiguationData":[TD([[makeQuery(id+"F0.imprint","IMPRINT",EDGE,{"derivedFrom":subQ3}),-1.0]])]});}
            var Q27;
            Q27=makeQuery(id+"F0.imprint","IMPRINT",FACE,{"disambiguationData":[TD([[makeQuery(id+"F0.imprint","IMPRINT",EDGE,{"derivedFrom":sQuery(id+"F0.wireOp",EDGE,"E9.0")}),1.0]])]});
            var Q28;
            {var subQ2=sQuery(id+"F0.wireOp",EDGE,"E13");Q28=makeQuery(id+"F0.imprint","IMPRINT",FACE,{"disambiguationData":[TD([[makeQuery(id+"F0.imprint","IMPRINT",EDGE,{"derivedFrom":subQ2}),1.0]])]});}
            var Q29;
            {var subQ1=sQuery(id+"F0.wireOp",EDGE,"E13");Q29=makeQuery(id+"F0.imprint","IMPRINT",FACE,{"disambiguationData":[TD([[makeQuery(id+"F0.imprint","IMPRINT",EDGE,{"derivedFrom":subQ1}),-1.0]])]});}
            var Q30;
            Q30=makeQuery(id+"F0.imprint","IMPRINT",FACE,{"disambiguationData":[TD([[makeQuery(id+"F0.imprint","IMPRINT",EDGE,{"derivedFrom":sQuery(id+"F0.wireOp",EDGE,"E18.0")}),1.0]])]});
            var Q31;
            {var subQ3=sQuery(id+"F0.wireOp",EDGE,"E22");Q31=makeQuery(id+"F0.imprint","IMPRINT",FACE,{"disambiguationData":[TD([[makeQuery(id+"F0.imprint","IMPRINT",EDGE,{"derivedFrom":subQ3}),-1.0]])]});}
            var Q32;
            Q32=makeQuery(id+"F0.imprint","IMPRINT",FACE,{"disambiguationData":[TD([[makeQuery(id+"F0.imprint","IMPRINT",EDGE,{"derivedFrom":sQuery(id+"F0.wireOp",EDGE,"E20.0")}),1.0]])]});
            var Q33;
            {var subQ2=sQuery(id+"F0.wireOp",EDGE,"E24");Q33=makeQuery(id+"F0.imprint","IMPRINT",FACE,{"disambiguationData":[TD([[makeQuery(id+"F0.imprint","IMPRINT",EDGE,{"derivedFrom":subQ2}),-1.0]])]});}
            var Q34;
            {var subQ1=sQuery(id+"F0.wireOp",EDGE,"E24");Q34=makeQuery(id+"F0.imprint","IMPRINT",FACE,{"disambiguationData":[TD([[makeQuery(id+"F0.imprint","IMPRINT",EDGE,{"derivedFrom":subQ1}),1.0]])]});}
            var Q35;
            Q35=makeQuery(id+"F0.imprint","IMPRINT",FACE,{"disambiguationData":[TD([[makeQuery(id+"F0.imprint","IMPRINT",EDGE,{"derivedFrom":sQuery(id+"F0.wireOp",EDGE,"E25.0")}),1.0]])]});
            var Q36;
            {var subQ7=sQuery(id+"F0.wireOp",EDGE,"E29");Q36=makeQuery(id+"F0.imprint","IMPRINT",FACE,{"disambiguationData":[TD([[makeQuery(id+"F0.imprint","IMPRINT",EDGE,{"derivedFrom":subQ7}),-1.0]])]});}
            var Q37;
            Q37=makeQuery(id+"F0.imprint","IMPRINT",FACE,{"disambiguationData":[TD([[makeQuery(id+"F0.imprint","IMPRINT",EDGE,{"derivedFrom":sQuery(id+"F0.wireOp",EDGE,"E27.0")}),1.0]])]});
            extrude(context, id + "F1", {"entities" : qUnion([Q0, Q1, Q2, Q3, Q4, Q5, Q6, Q7, Q8, Q9, Q10, Q11, Q12, Q13, Q14, Q15, Q16, Q17, Q18, Q19, Q20, Q21, Q22, Q23, Q24, Q25, Q26, Q27, Q28, Q29, Q30, Q31, Q32, Q33, Q34, Q35, Q36, Q37]), "depth" : 0.7 * mm, "offsetDistance" : 25 * mm});
        }
    });
